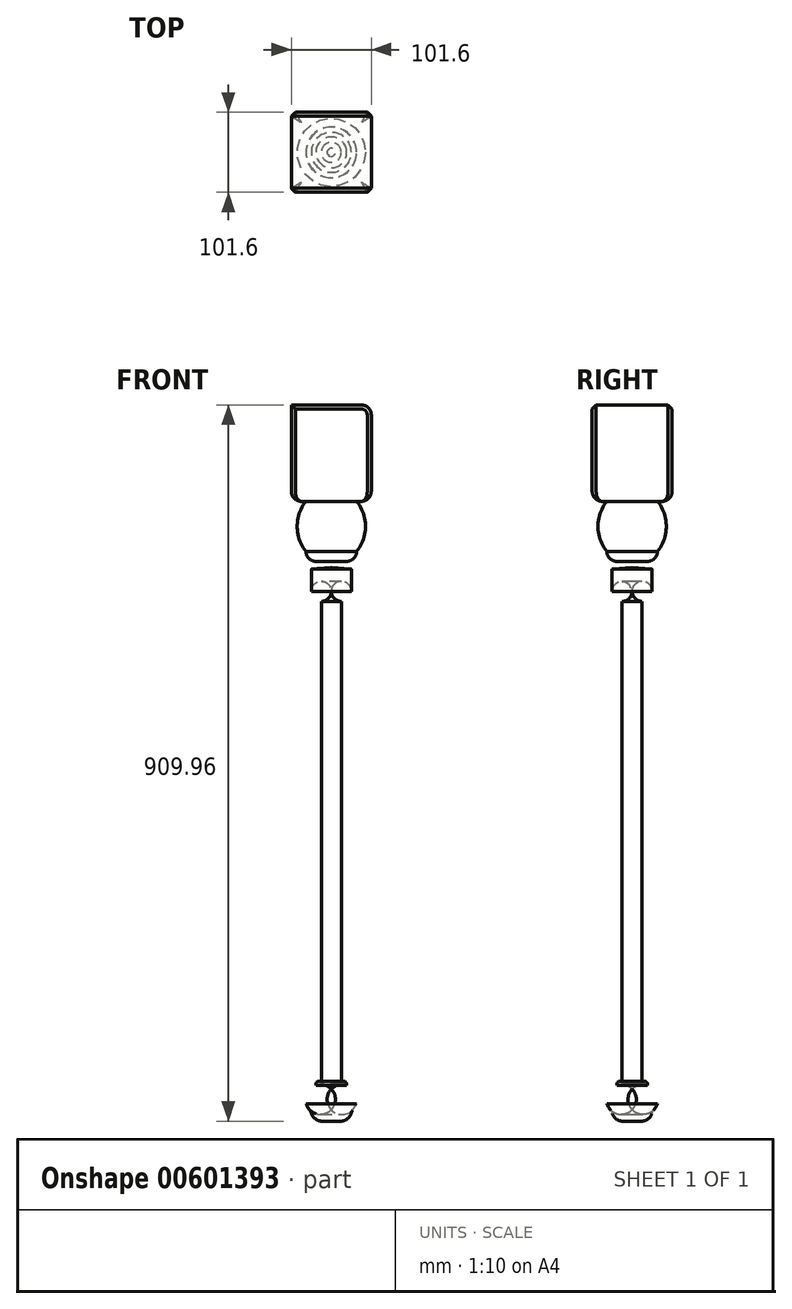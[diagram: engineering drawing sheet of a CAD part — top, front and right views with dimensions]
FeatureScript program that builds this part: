
annotation { "Feature Type Name" : "Feature", "Feature Type Description" : "" }
export const myFeature = defineFeature(function(context is Context, id is Id, definition is map)
    precondition{}
    {
        {
            var Q0;
            Q0=qCreatedBy(makeId("Front.planeOp"),FACE);
            var sketch = newSketch(context, id + "F0", { "sketchPlane" : qUnion([Q0])});
            skLineSegment(sketch, "E0.bottom", {"start": v(-9.66, 55.8) * mm, "end": v(22.57, 55.8) * mm});
            skLineSegment(sketch, "E0.top", {"start": v(-9.66, -20.4) * mm, "end": v(9.87, -20.4) * mm});
            skLineSegment(sketch, "E1.bottom", {"start": v(-9.66, -20.4) * mm, "end": v(15.74, -20.4) * mm});
            skLineSegment(sketch, "E1.left", {"start": v(-35.06, -23.57) * mm, "end": v(-35.06, -26.74) * mm});
            skLineSegment(sketch, "E1.right", {"start": v(15.74, -30.25) * mm, "end": v(15.74, -58.5) * mm});
            skPoint(sketch, "E2.visualSharp", {"position": v(22.57, -20.4) * mm});
            skArc(sketch, "E2.filletArc", {"start": v(9.87, -20.4) * mm, "mid": v(18.85, -16.67) * mm, "end": v(22.57, -7.7) * mm});
            skPoint(sketch, "E3.visualSharp", {"position": v(-47.76, -20.4) * mm});
            skPoint(sketch, "E4.visualSharp", {"position": v(15.74, -71.2) * mm});
            skArc(sketch, "E4.filletArc", {"start": v(3.04, -71.2) * mm, "mid": v(12.03, -67.47) * mm, "end": v(15.74, -58.5) * mm});
            skPoint(sketch, "E5.visualSharp", {"position": v(-35.06, -71.2) * mm});
            skLineSegment(sketch, "E6", {"start": v(-9.66, 55.8) * mm, "end": v(-9.66, -71.2) * mm});
            skArc(sketch, "E7", {"start": v(9.87, -20.4) * mm, "mid": v(10, -27) * mm, "end": v(15.74, -30.25) * mm});
            skArc(sketch, "E8", {"start": v(-35.06, -26.74) * mm, "mid": v(-31.88, -23.57) * mm, "end": v(-35.06, -20.4) * mm});
            skLineSegment(sketch, "E9", {"start": v(-9.66, -28.5) * mm, "end": v(15.74, -30.25) * mm});
            skLineSegment(sketch, "E10.left", {"start": v(-9.66, -71.2) * mm, "end": v(-9.66, -680.8) * mm});
            skLineSegment(sketch, "E10.right", {"start": v(3.04, -71.2) * mm, "end": v(3.04, -680.8) * mm});
            skLineSegment(sketch, "E11.bottom", {"start": v(3.04, -680.8) * mm, "end": v(9.4, -680.8) * mm});
            skLineSegment(sketch, "E11.top", {"start": v(-9.66, -731.6) * mm, "end": v(2.18, -731.6) * mm});
            skLineSegment(sketch, "E11.left", {"start": v(-9.66, -680.8) * mm, "end": v(-9.66, -731.6) * mm});
            skLineSegment(sketch, "E12", {"start": v(9.4, -680.8) * mm, "end": v(9.87, -685.8) * mm});
            skPoint(sketch, "E13.orphan", {"position": v(28.44, -680.8) * mm});
            skPoint(sketch, "E14.visualSharp", {"position": v(22.68, -686.48) * mm});
            skArc(sketch, "E14.filletArc", {"start": v(22.1, -710.23) * mm, "mid": v(21.15, -695.43) * mm, "end": v(9.87, -685.8) * mm});
            skArc(sketch, "E15", {"start": v(22.1, -710.23) * mm, "mid": v(18.2, -715.84) * mm, "end": v(15.41, -722.09) * mm});
            skPoint(sketch, "E16.orphan", {"position": v(38.15, -731.6) * mm});
            skPoint(sketch, "E17.visualSharp", {"position": v(13.57, -731.6) * mm});
            skArc(sketch, "E17.filletArc", {"start": v(2.18, -731.6) * mm, "mid": v(10.33, -728.97) * mm, "end": v(15.41, -722.09) * mm});
            skPoint(sketch, "E18.orphan", {"position": v(14.25, -731.6) * mm});
            skPoint(sketch, "E5.filletArc.end.orphan", {"position": v(-22.36, -71.2) * mm});
            skPoint(sketch, "E19.orphan", {"position": v(-35.06, -20.4) * mm});
            skPoint(sketch, "E20.orphan", {"position": v(-41.88, 55.8) * mm});
            skLineSegment(sketch, "E21.bottom", {"start": v(-60.46, 178.37) * mm, "end": v(41.14, 178.37) * mm});
            skLineSegment(sketch, "E21.top", {"start": v(-9.66, -66.76) * mm, "end": v(12.69, -66.76) * mm});
            skPoint(sketch, "E21.middle", {"position": v(-9.66, 55.8) * mm});
            skLineSegment(sketch, "E22", {"start": v(22.57, 55.8) * mm, "end": v(41.14, 55.8) * mm});
            skLineSegment(sketch, "E23", {"start": v(41.14, 55.8) * mm, "end": v(-60.46, 55.8) * mm});
            skPoint(sketch, "E24.orphan", {"position": v(86.07, -66.76) * mm});
            skPoint(sketch, "E25.orphan", {"position": v(-105.38, -66.76) * mm});
            skLineSegment(sketch, "E26", {"start": v(41.14, 178.37) * mm, "end": v(41.14, 55.8) * mm});
            skPoint(sketch, "E21.right.start.orphan", {"position": v(86.07, 178.37) * mm});
            skPoint(sketch, "E27.orphan", {"position": v(86.07, 55.8) * mm});
            skLineSegment(sketch, "E28", {"start": v(-60.46, 55.8) * mm, "end": v(-60.46, 178.37) * mm});
            skPoint(sketch, "E21.left.start.orphan", {"position": v(-105.38, 178.37) * mm});
            skPoint(sketch, "E29.orphan", {"position": v(-105.38, 55.8) * mm});
            skArc(sketch, "E30", {"start": v(22.57, -7.7) * mm, "mid": v(33.71, 24.06) * mm, "end": v(22.57, 55.8) * mm});
            skSolve(sketch);
        }
        {
            var Q0;
            {var subQ1=sQuery(id+"F0.wireOp",EDGE,"E0.left");Q0=makeQuery(id+"F0.imprint","IMPRINT",FACE,{"disambiguationData":[TD([[makeQuery(id+"F0.imprint","IMPRINT",EDGE,{"derivedFrom":subQ1}),1.0]])]});}
            var Q1;
            {var subQ0=sQuery(id+"F0.wireOp",EDGE,"E5.filletArc");Q1=makeQuery(id+"F0.imprint","IMPRINT",FACE,{"disambiguationData":[TD([[makeQuery(id+"F0.imprint","IMPRINT",EDGE,{"derivedFrom":subQ0}),1.0]])]});}
            var Q2;
            {var subQ0=sQuery(id+"F0.wireOp",EDGE,"E8");Q2=makeQuery(id+"F0.imprint","IMPRINT",FACE,{"disambiguationData":[TD([[makeQuery(id+"F0.imprint","IMPRINT",EDGE,{"derivedFrom":subQ0}),-1.0]])]});}
            var Q3;
            Q3=makeQuery(id+"F0.imprint","IMPRINT",FACE,{"disambiguationData":[TD([[makeQuery(id+"F0.imprint","IMPRINT",EDGE,{"derivedFrom":sQuery(id+"F0.wireOp",EDGE,"E10.bottom")}),-1.0]])]});
            var Q4;
            {var subQ0=sQuery(id+"F0.wireOp",EDGE,"E11.left");Q4=makeQuery(id+"F0.imprint","IMPRINT",FACE,{"disambiguationData":[TD([[makeQuery(id+"F0.imprint","IMPRINT",EDGE,{"derivedFrom":subQ0}),1.0]])]});}
            var Q5;
            {var subQ0=sQuery(id+"F0.wireOp",EDGE,"lPBJvOPI-qiMk-AvVH-LaXD-WZ1mESJmoz4I");Q5=makeQuery(id+"F0.imprint","IMPRINT",FACE,{"disambiguationData":[TD([[makeQuery(id+"F0.imprint","IMPRINT",EDGE,{"derivedFrom":subQ0}),-1.0]])]});}
            var Q6;
            {var subQ1=sQuery(id+"F0.wireOp",EDGE,"E0.bottom");Q6=makeQuery(id+"F0.imprint","IMPRINT",FACE,{"disambiguationData":[TD([[makeQuery(id+"F0.imprint","IMPRINT",EDGE,{"derivedFrom":subQ1}),-1.0]])]});}
            var Q7;
            {var subQ0=sQuery(id+"F0.wireOp",EDGE,"E1.bottom");Q7=makeQuery(id+"F0.imprint","IMPRINT",FACE,{"disambiguationData":[TD([[makeQuery(id+"F0.imprint","IMPRINT",EDGE,{"derivedFrom":subQ0}),-1.0]])]});}
            var Q8;
            {var subQ2=sQuery(id+"F0.wireOp",EDGE,"E1.right");Q8=makeQuery(id+"F0.imprint","IMPRINT",FACE,{"disambiguationData":[TD([[makeQuery(id+"F0.imprint","IMPRINT",EDGE,{"derivedFrom":subQ2}),-1.0]])]});}
            var Q9;
            {var subQ6=sQuery(id+"F0.wireOp",EDGE,"E0.right");Q9=makeQuery(id+"F0.imprint","IMPRINT",FACE,{"disambiguationData":[TD([[makeQuery(id+"F0.imprint","IMPRINT",EDGE,{"derivedFrom":subQ6}),-1.0]])]});}
            var Q10;
            {var subQ0=sQuery(id+"F0.wireOp",EDGE,"E2.filletArc");Q10=makeQuery(id+"F0.imprint","IMPRINT",FACE,{"disambiguationData":[TD([[makeQuery(id+"F0.imprint","IMPRINT",EDGE,{"derivedFrom":subQ0}),1.0]])]});}
            var Q11;
            Q11=sQuery(id+"F0.wireOp",EDGE,"E6");
            revolve(context, id + "F1", {"entities" : qUnion([Q0, Q1, Q2, Q3, Q4, Q5, Q6, Q7, Q8, Q9, Q10]), "axis" : qUnion([Q11]), "revolveType" : RevolveType.SYMMETRIC, "angle" : 360 * degree});
        }
        {
            var Q0;
            Q0=makeQuery(id+"F1.opRevolve","SWEPT_EDGE",EDGE,{"disambiguationData":[OSD([sQuery(id+"F0.wireOp",EDGE,"E1.left"),sQuery(id+"F0.wireOp",EDGE,"E8"),sQuery(id+"F0.wireOp",EDGE,"E9")])]});
            var Q1;
            Q1=makeQuery(id+"F1.opRevolve","SWEPT_EDGE",EDGE,{"disambiguationData":[OSD([sQuery(id+"F0.wireOp",EDGE,"E14.filletArc"),sQuery(id+"F0.wireOp",EDGE,"E15")])]});
            var Q2;
            Q2=makeQuery(id+"F1.opRevolve","SWEPT_EDGE",EDGE,{"disambiguationData":[OSD([sQuery(id+"F0.wireOp",EDGE,"E15"),sQuery(id+"F0.wireOp",EDGE,"E17.filletArc")])]});
            var Q3;
            Q3=makeQuery(id+"F1.opRevolve","SWEPT_EDGE",EDGE,{"disambiguationData":[OSD([sQuery(id+"F0.wireOp",EDGE,"E11.bottom"),sQuery(id+"F0.wireOp",EDGE,"E12")])]});
            fillet(context, id + "F2", {"entities" : qUnion([Q0, Q1, Q2, Q3]), "radius" : 3.5 * mm, "tangentPropagation" : true, "allowEdgeOverflow" : false});
        }
        {
            var Q0;
            Q0=makeQuery(id+"F0.imprint","IMPRINT",FACE,{"disambiguationData":[TD([[makeQuery(id+"F0.imprint","IMPRINT",EDGE,{"derivedFrom":sQuery(id+"F0.wireOp",EDGE,"E21.bottom")}),-1.0]])]});
            extrude(context, id + "F3", {"entities" : qUnion([Q0]), "operationType" : NewBodyOperationType.ADD, "endBound" : BoundingType.SYMMETRIC, "depth" : 101.6 * mm, "offsetDistance" : 25.4 * mm});
        }
        {
            var Q0;
            Q0=makeQuery(id+"F3.opExtrude","SWEPT_EDGE",EDGE,{"disambiguationData":[OSD([sQuery(id+"F0.wireOp",EDGE,"E23"),sQuery(id+"F0.wireOp",EDGE,"E26")])]});
            var Q1;
            Q1=makeQuery(id+"F3.opExtrude","CAP_EDGE",EDGE,{"disambiguationData":[OSD([sQuery(id+"F0.wireOp",EDGE,"E23")])],"isStart":false});
            var Q2;
            Q2=makeQuery(id+"F3.opExtrude","SWEPT_EDGE",EDGE,{"disambiguationData":[OSD([sQuery(id+"F0.wireOp",EDGE,"E23"),sQuery(id+"F0.wireOp",EDGE,"E28")])]});
            var Q3;
            Q3=makeQuery(id+"F3.opExtrude","CAP_EDGE",EDGE,{"disambiguationData":[OSD([sQuery(id+"F0.wireOp",EDGE,"E23")])],"isStart":true});
            fillet(context, id + "F4", {"entities" : qUnion([Q0, Q1, Q2, Q3]), "radius" : 12.7 * mm, "tangentPropagation" : true, "allowEdgeOverflow" : false});
        }
        {
            var Q0;
            Q0=makeQuery(id+"F3.opExtrude","CAP_EDGE",EDGE,{"disambiguationData":[OSD([sQuery(id+"F0.wireOp",EDGE,"E28")])],"isStart":false});
            var Q1;
            Q1=makeQuery(id+"F3.opExtrude","CAP_EDGE",EDGE,{"disambiguationData":[OSD([sQuery(id+"F0.wireOp",EDGE,"E26")])],"isStart":false});
            var Q2;
            Q2=makeQuery(id+"F3.opExtrude","CAP_EDGE",EDGE,{"disambiguationData":[OSD([sQuery(id+"F0.wireOp",EDGE,"E26")])],"isStart":true});
            var Q3;
            Q3=makeQuery(id+"F3.opExtrude","CAP_EDGE",EDGE,{"disambiguationData":[OSD([sQuery(id+"F0.wireOp",EDGE,"E28")])],"isStart":true});
            chamfer(context, id + "F5", {"entities" : qUnion([Q0, Q1, Q2, Q3]), "width" : 5.08 * mm, "tangentPropagation" : true});
        }
    });
